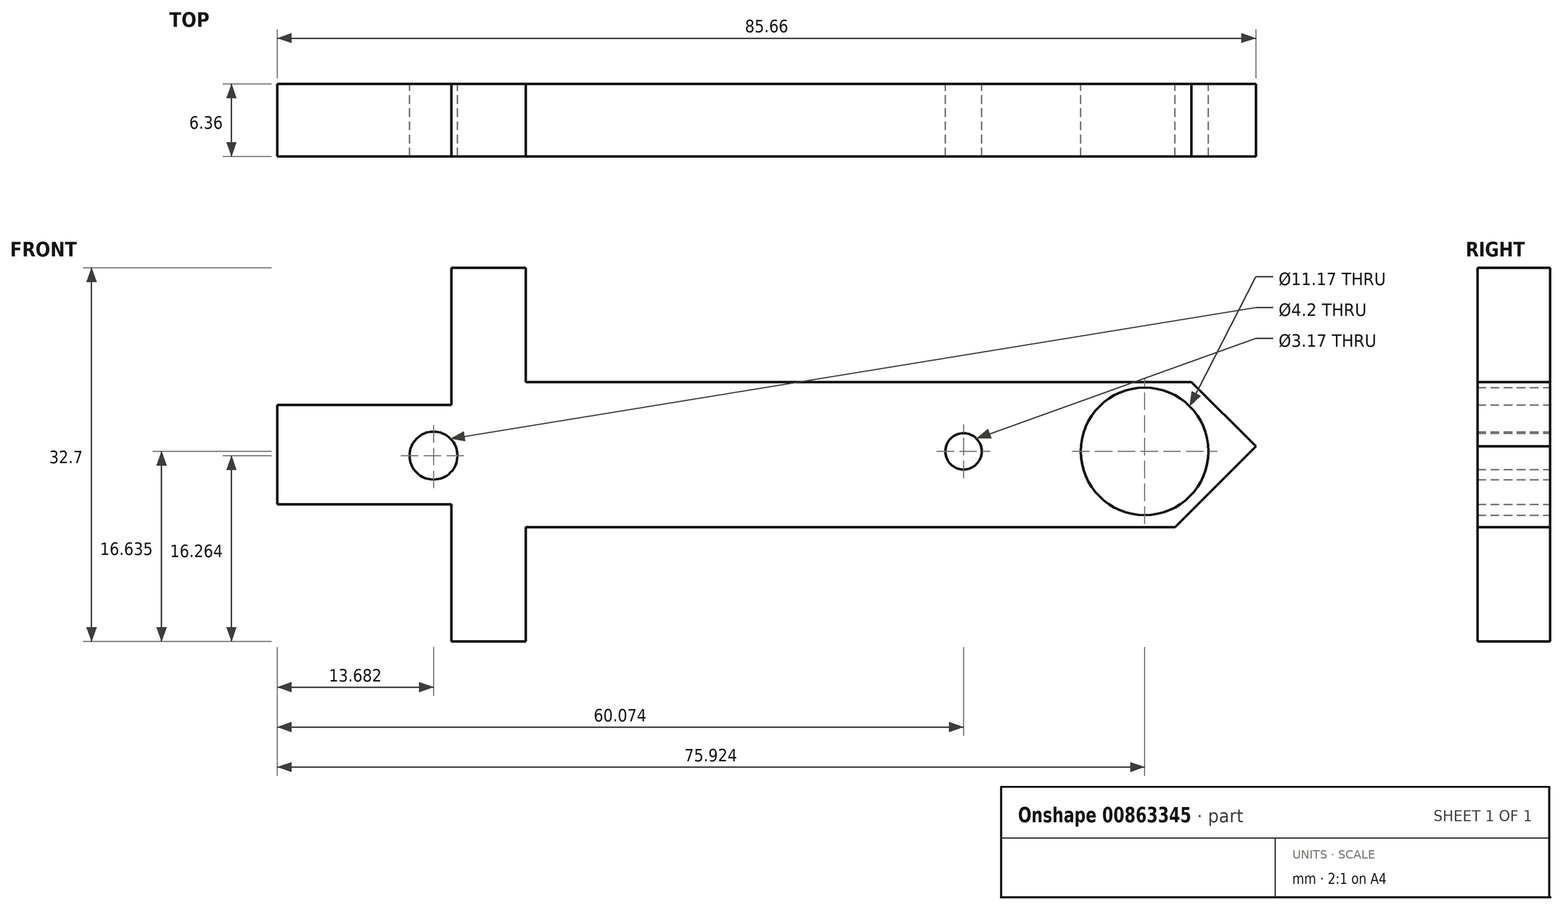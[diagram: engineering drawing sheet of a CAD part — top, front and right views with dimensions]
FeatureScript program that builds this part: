
annotation { "Feature Type Name" : "Feature", "Feature Type Description" : "" }
export const myFeature = defineFeature(function(context is Context, id is Id, definition is map)
    precondition{}
    {
        {
            var Q0;
            Q0=qCreatedBy(makeId("Front.planeOp"),FACE);
            var sketch = newSketch(context, id + "F0", { "sketchPlane" : qUnion([Q0])});
            skLineSegment(sketch, "E0", {"start": v(1.44, 0) * mm, "end": v(-46.82, 0) * mm});
            skLineSegment(sketch, "E1", {"start": v(0, -12.7) * mm, "end": v(-46.82, -12.7) * mm});
            skLineSegment(sketch, "E2", {"start": v(-46.82, -12.7) * mm, "end": v(-46.82, -22.7) * mm});
            skLineSegment(sketch, "E3", {"start": v(-46.82, -22.7) * mm, "end": v(-53.35, -22.7) * mm});
            skLineSegment(sketch, "E4", {"start": v(-46.82, 0) * mm, "end": v(-46.82, 10) * mm});
            skLineSegment(sketch, "E5", {"start": v(-46.82, 10) * mm, "end": v(-53.35, 10) * mm});
            skLineSegment(sketch, "E6", {"start": v(-53.35, 10) * mm, "end": v(-53.35, -2) * mm});
            skLineSegment(sketch, "E7", {"start": v(-53.35, -22.7) * mm, "end": v(-53.35, -10.7) * mm});
            skLineSegment(sketch, "E8", {"start": v(-53.35, -10.7) * mm, "end": v(-68.59, -10.7) * mm});
            skLineSegment(sketch, "E9", {"start": v(-53.35, -2) * mm, "end": v(-68.59, -2) * mm});
            skLineSegment(sketch, "E10", {"start": v(-68.59, -2) * mm, "end": v(-68.59, -10.7) * mm});
            skLineSegment(sketch, "E11", {"start": v(-46.82, 0) * mm, "end": v(-46.82, -12.7) * mm});
            skCircle(sketch, "E12", {"center": v(-54.9, -6.44) * mm, "radius": 2.1 * mm});
            skCircle(sketch, "E13", {"center": v(-8.52, -6.06) * mm, "radius": 1.59 * mm});
            skLineSegment(sketch, "E14", {"start": v(1.44, 0) * mm, "end": v(11.44, 0) * mm});
            skLineSegment(sketch, "E15", {"start": v(0, -12.7) * mm, "end": v(10, -12.7) * mm});
            skLineSegment(sketch, "E16", {"start": v(10, -12.7) * mm, "end": v(17.07, -5.63) * mm});
            skLineSegment(sketch, "E17", {"start": v(17.07, -5.63) * mm, "end": v(11.44, 0) * mm});
            skPoint(sketch, "E18.middle", {"position": v(7.33, -6.06) * mm});
            skCircle(sketch, "E19", {"center": v(7.33, -6.06) * mm, "radius": 5.58 * mm});
            skSolve(sketch);
        }
        {
            var Q0;
            Q0=makeQuery(id+"F0.imprint","IMPRINT",FACE,{"disambiguationData":[TD([[makeQuery(id+"F0.imprint","IMPRINT",EDGE,{"derivedFrom":sQuery(id+"F0.wireOp",EDGE,"E2")}),-1.0]])]});
            var Q1;
            Q1=makeQuery(id+"F0.imprint","IMPRINT",FACE,{"disambiguationData":[TD([[makeQuery(id+"F0.imprint","IMPRINT",EDGE,{"derivedFrom":sQuery(id+"F0.wireOp",EDGE,"E0")}),1.0]])]});
            extrude(context, id + "F1", {"entities" : qUnion([Q0, Q1]), "endBound" : BoundingType.SYMMETRIC, "depth" : 6.35 * mm, "offsetDistance" : 25 * mm});
        }
    });
